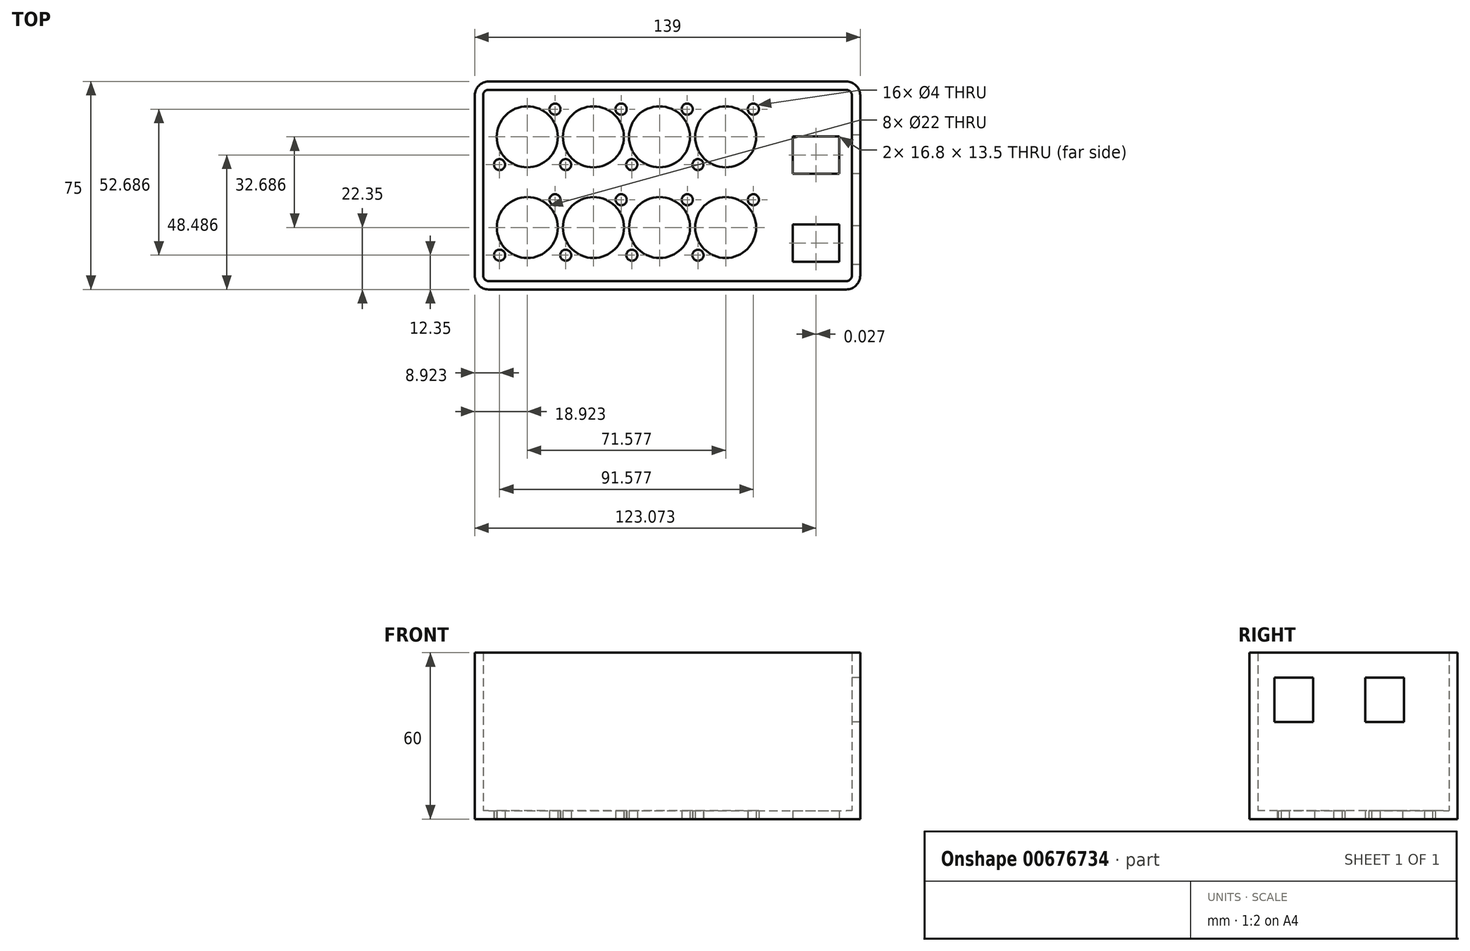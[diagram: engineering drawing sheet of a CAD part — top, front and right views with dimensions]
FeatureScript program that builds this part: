
annotation { "Feature Type Name" : "Feature", "Feature Type Description" : "" }
export const myFeature = defineFeature(function(context is Context, id is Id, definition is map)
    precondition{}
    {
        {
            var Q0;
            Q0=qCreatedBy(makeId("Top.planeOp"),FACE);
            var sketch = newSketch(context, id + "F0", { "sketchPlane" : qUnion([Q0])});
            skLineSegment(sketch, "E0.bottom", {"start": v(63.5, 18.5) * mm, "end": v(-63.5, 18.5) * mm, "construction": true});
            skLineSegment(sketch, "E0.top", {"start": v(66.5, -18.5) * mm, "end": v(-66.5, -18.5) * mm});
            skLineSegment(sketch, "E0.left", {"start": v(66.5, 15.5) * mm, "end": v(66.5, -18.5) * mm});
            skLineSegment(sketch, "E0.right", {"start": v(-66.5, 15.5) * mm, "end": v(-66.5, -18.5) * mm});
            skPoint(sketch, "E0.middle", {"position": v(0, 0) * mm});
            skLineSegment(sketch, "E1.top", {"start": v(45.2, 2) * mm, "end": v(62, 2) * mm});
            skCircle(sketch, "E2", {"center": v(21, 0.85) * mm, "radius": 11 * mm});
            skCircle(sketch, "E3", {"center": v(31, 10.85) * mm, "radius": 2 * mm});
            skCircle(sketch, "E4", {"center": v(11, -9.15) * mm, "radius": 2 * mm});
            skLineSegment(sketch, "E5", {"start": v(21, 0.85) * mm, "end": v(31, 10.85) * mm, "construction": true});
            skLineSegment(sketch, "E6", {"start": v(21, 0.85) * mm, "end": v(11, -9.15) * mm, "construction": true});
            skCircle(sketch, "E7", {"center": v(38.45, -6.1) * mm, "radius": 3.5 * mm, "construction": true});
            skLineSegment(sketch, "E8", {"start": v(64.5, -11.5) * mm, "end": v(-64.5, -11.5) * mm, "construction": true});
            skLineSegment(sketch, "E9.bottom", {"start": v(26.2, 19.15) * mm, "end": v(15.8, 19.15) * mm, "construction": true});
            skPoint(sketch, "E9.middle", {"position": v(21, 11.85) * mm});
            skLineSegment(sketch, "E10", {"start": v(15.8, 19.15) * mm, "end": v(15.8, 11.85) * mm, "construction": true});
            skLineSegment(sketch, "E11", {"start": v(15.8, 11.85) * mm, "end": v(15.8, 10.54) * mm, "construction": true});
            skLineSegment(sketch, "E12", {"start": v(15.8, 10.54) * mm, "end": v(26.2, 10.54) * mm, "construction": true});
            skLineSegment(sketch, "E13", {"start": v(26.2, 19.15) * mm, "end": v(26.2, 11.85) * mm, "construction": true});
            skLineSegment(sketch, "E14", {"start": v(26.2, 11.85) * mm, "end": v(26.2, 10.54) * mm, "construction": true});
            skCircle(sketch, "E15", {"center": v(21, -3.8) * mm, "radius": 6.5 * mm, "construction": true});
            skCircle(sketch, "E16.1.0.0", {"center": v(-2.85, -3.8) * mm, "radius": 6.5 * mm, "construction": true});
            skLineSegment(sketch, "E16.1.0.1", {"start": v(-2.85, 0.85) * mm, "end": v(7.15, 10.85) * mm, "construction": true});
            skLineSegment(sketch, "E16.1.0.2", {"start": v(2.35, 19.15) * mm, "end": v(-8.05, 19.15) * mm, "construction": true});
            skLineSegment(sketch, "E16.1.0.3", {"start": v(-2.85, 0.85) * mm, "end": v(-12.85, -9.15) * mm, "construction": true});
            skPoint(sketch, "E16.1.0.4", {"position": v(-2.85, 11.85) * mm});
            skLineSegment(sketch, "E16.1.0.5", {"start": v(2.35, 19.15) * mm, "end": v(2.35, 11.85) * mm, "construction": true});
            skCircle(sketch, "E16.1.0.6", {"center": v(-2.85, 0.85) * mm, "radius": 11 * mm});
            skCircle(sketch, "E16.1.0.7", {"center": v(7.15, 10.85) * mm, "radius": 2 * mm});
            skCircle(sketch, "E16.1.0.8", {"center": v(-12.85, -9.15) * mm, "radius": 2 * mm});
            skLineSegment(sketch, "E16.1.0.9", {"start": v(-8.05, 10.54) * mm, "end": v(2.35, 10.54) * mm, "construction": true});
            skLineSegment(sketch, "E16.1.0.10", {"start": v(-8.05, 19.15) * mm, "end": v(-8.05, 11.85) * mm, "construction": true});
            skLineSegment(sketch, "E16.1.0.11", {"start": v(2.35, 11.85) * mm, "end": v(2.35, 10.54) * mm, "construction": true});
            skLineSegment(sketch, "E16.1.0.12", {"start": v(-8.05, 11.85) * mm, "end": v(-8.05, 10.54) * mm, "construction": true});
            skCircle(sketch, "E16.2.0.0", {"center": v(-26.7, -3.8) * mm, "radius": 6.5 * mm, "construction": true});
            skLineSegment(sketch, "E16.2.0.1", {"start": v(-26.7, 0.85) * mm, "end": v(-16.7, 10.85) * mm, "construction": true});
            skLineSegment(sketch, "E16.2.0.2", {"start": v(-21.5, 19.15) * mm, "end": v(-31.9, 19.15) * mm, "construction": true});
            skLineSegment(sketch, "E16.2.0.3", {"start": v(-26.7, 0.85) * mm, "end": v(-36.7, -9.15) * mm, "construction": true});
            skPoint(sketch, "E16.2.0.4", {"position": v(-26.7, 11.85) * mm});
            skLineSegment(sketch, "E16.2.0.5", {"start": v(-21.5, 19.15) * mm, "end": v(-21.5, 11.85) * mm, "construction": true});
            skCircle(sketch, "E16.2.0.6", {"center": v(-26.7, 0.85) * mm, "radius": 11 * mm});
            skCircle(sketch, "E16.2.0.7", {"center": v(-16.7, 10.85) * mm, "radius": 2 * mm});
            skCircle(sketch, "E16.2.0.8", {"center": v(-36.7, -9.15) * mm, "radius": 2 * mm});
            skLineSegment(sketch, "E16.2.0.9", {"start": v(-31.9, 10.54) * mm, "end": v(-21.5, 10.54) * mm, "construction": true});
            skLineSegment(sketch, "E16.2.0.10", {"start": v(-31.9, 19.15) * mm, "end": v(-31.9, 11.85) * mm, "construction": true});
            skLineSegment(sketch, "E16.2.0.11", {"start": v(-21.5, 11.85) * mm, "end": v(-21.5, 10.54) * mm, "construction": true});
            skLineSegment(sketch, "E16.2.0.12", {"start": v(-31.9, 11.85) * mm, "end": v(-31.9, 10.54) * mm, "construction": true});
            skCircle(sketch, "E16.3.0.0", {"center": v(-50.55, -3.8) * mm, "radius": 6.5 * mm, "construction": true});
            skLineSegment(sketch, "E16.3.0.1", {"start": v(-50.55, 0.85) * mm, "end": v(-40.55, 10.85) * mm, "construction": true});
            skLineSegment(sketch, "E16.3.0.2", {"start": v(-45.35, 19.15) * mm, "end": v(-55.75, 19.15) * mm, "construction": true});
            skLineSegment(sketch, "E16.3.0.3", {"start": v(-50.55, 0.85) * mm, "end": v(-60.55, -9.15) * mm, "construction": true});
            skPoint(sketch, "E16.3.0.4", {"position": v(-50.55, 11.85) * mm});
            skLineSegment(sketch, "E16.3.0.5", {"start": v(-45.35, 19.15) * mm, "end": v(-45.35, 11.85) * mm, "construction": true});
            skCircle(sketch, "E16.3.0.6", {"center": v(-50.55, 0.85) * mm, "radius": 11 * mm});
            skCircle(sketch, "E16.3.0.7", {"center": v(-40.55, 10.85) * mm, "radius": 2 * mm});
            skCircle(sketch, "E16.3.0.8", {"center": v(-60.55, -9.15) * mm, "radius": 2 * mm});
            skLineSegment(sketch, "E16.3.0.9", {"start": v(-55.75, 10.54) * mm, "end": v(-45.35, 10.54) * mm, "construction": true});
            skLineSegment(sketch, "E16.3.0.10", {"start": v(-55.75, 19.15) * mm, "end": v(-55.75, 11.85) * mm, "construction": true});
            skLineSegment(sketch, "E16.3.0.11", {"start": v(-45.35, 11.85) * mm, "end": v(-45.35, 10.54) * mm, "construction": true});
            skLineSegment(sketch, "E16.3.0.12", {"start": v(-55.75, 11.85) * mm, "end": v(-55.75, 10.54) * mm, "construction": true});
            skLineSegment(sketch, "E16.direction1", {"start": v(21, 0.85) * mm, "end": v(-2.85, 0.85) * mm, "construction": true});
            skLineSegment(sketch, "E17.0", {"start": v(63.5, 21.5) * mm, "end": v(-63.5, 21.5) * mm, "construction": true});
            skLineSegment(sketch, "E17.1", {"start": v(69.5, 15.5) * mm, "end": v(69.5, -15.5) * mm});
            skLineSegment(sketch, "E17.2", {"start": v(63.5, -21.5) * mm, "end": v(-63.5, -21.5) * mm});
            skLineSegment(sketch, "E17.3", {"start": v(-69.5, 15.5) * mm, "end": v(-69.5, -15.5) * mm});
            skPoint(sketch, "E18.visualSharp", {"position": v(-69.5, 21.5) * mm});
            skPoint(sketch, "E19.visualSharp", {"position": v(69.5, 21.5) * mm});
            skPoint(sketch, "E20.visualSharp", {"position": v(66.5, 18.5) * mm});
            skPoint(sketch, "E21.visualSharp", {"position": v(-69.5, -21.5) * mm});
            skPoint(sketch, "E22.visualSharp", {"position": v(69.5, -21.5) * mm});
            skLineSegment(sketch, "E23", {"start": v(45.2, 2) * mm, "end": v(45.2, -11.5) * mm});
            skLineSegment(sketch, "E24", {"start": v(45.2, -11.5) * mm, "end": v(62, -11.5) * mm});
            skLineSegment(sketch, "E25", {"start": v(62, -11.5) * mm, "end": v(62, 2) * mm});
            skPoint(sketch, "E26.middle", {"position": v(-0.03, 32.69) * mm});
            skLineSegment(sketch, "E27.top", {"start": v(45.17, 33.74) * mm, "end": v(61.97, 33.74) * mm});
            skCircle(sketch, "E28", {"center": v(20.97, 33.54) * mm, "radius": 11 * mm});
            skCircle(sketch, "E29", {"center": v(30.97, 43.54) * mm, "radius": 2 * mm});
            skCircle(sketch, "E30", {"center": v(10.97, 23.54) * mm, "radius": 2 * mm});
            skLineSegment(sketch, "E31", {"start": v(20.97, 33.54) * mm, "end": v(30.97, 43.54) * mm, "construction": true});
            skLineSegment(sketch, "E32", {"start": v(20.97, 33.54) * mm, "end": v(10.97, 23.54) * mm, "construction": true});
            skCircle(sketch, "E33", {"center": v(38.42, 26.59) * mm, "radius": 3.5 * mm, "construction": true});
            skPoint(sketch, "E34.middle", {"position": v(20.97, 44.54) * mm});
            skLineSegment(sketch, "E35", {"start": v(15.77, 44.54) * mm, "end": v(15.77, 43.23) * mm, "construction": true});
            skLineSegment(sketch, "E36", {"start": v(15.77, 43.23) * mm, "end": v(26.17, 43.23) * mm, "construction": true});
            skLineSegment(sketch, "E37", {"start": v(26.17, 44.54) * mm, "end": v(26.17, 43.23) * mm, "construction": true});
            skCircle(sketch, "E38", {"center": v(20.97, 28.89) * mm, "radius": 6.5 * mm, "construction": true});
            skCircle(sketch, "E39.1.0.0", {"center": v(-2.88, 28.89) * mm, "radius": 6.5 * mm, "construction": true});
            skLineSegment(sketch, "E39.1.0.1", {"start": v(-2.88, 33.54) * mm, "end": v(7.12, 43.54) * mm, "construction": true});
            skLineSegment(sketch, "E39.1.0.3", {"start": v(-2.88, 33.54) * mm, "end": v(-12.88, 23.54) * mm, "construction": true});
            skPoint(sketch, "E39.1.0.4", {"position": v(-2.88, 44.54) * mm});
            skCircle(sketch, "E39.1.0.6", {"center": v(-2.88, 33.54) * mm, "radius": 11 * mm});
            skCircle(sketch, "E39.1.0.7", {"center": v(7.12, 43.54) * mm, "radius": 2 * mm});
            skCircle(sketch, "E39.1.0.8", {"center": v(-12.88, 23.54) * mm, "radius": 2 * mm});
            skLineSegment(sketch, "E39.1.0.9", {"start": v(-8.08, 43.23) * mm, "end": v(2.32, 43.23) * mm, "construction": true});
            skLineSegment(sketch, "E39.1.0.11", {"start": v(2.32, 44.54) * mm, "end": v(2.32, 43.23) * mm, "construction": true});
            skLineSegment(sketch, "E39.1.0.12", {"start": v(-8.08, 44.54) * mm, "end": v(-8.08, 43.23) * mm, "construction": true});
            skCircle(sketch, "E39.2.0.0", {"center": v(-26.73, 28.89) * mm, "radius": 6.5 * mm, "construction": true});
            skLineSegment(sketch, "E39.2.0.1", {"start": v(-26.73, 33.54) * mm, "end": v(-16.73, 43.54) * mm, "construction": true});
            skLineSegment(sketch, "E39.2.0.3", {"start": v(-26.73, 33.54) * mm, "end": v(-36.73, 23.54) * mm, "construction": true});
            skPoint(sketch, "E39.2.0.4", {"position": v(-26.73, 44.54) * mm});
            skCircle(sketch, "E39.2.0.6", {"center": v(-26.73, 33.54) * mm, "radius": 11 * mm});
            skCircle(sketch, "E39.2.0.7", {"center": v(-16.73, 43.54) * mm, "radius": 2 * mm});
            skCircle(sketch, "E39.2.0.8", {"center": v(-36.73, 23.54) * mm, "radius": 2 * mm});
            skLineSegment(sketch, "E39.2.0.9", {"start": v(-31.93, 43.23) * mm, "end": v(-21.53, 43.23) * mm, "construction": true});
            skLineSegment(sketch, "E39.2.0.11", {"start": v(-21.53, 44.54) * mm, "end": v(-21.53, 43.23) * mm, "construction": true});
            skLineSegment(sketch, "E39.2.0.12", {"start": v(-31.93, 44.54) * mm, "end": v(-31.93, 43.23) * mm, "construction": true});
            skCircle(sketch, "E39.3.0.0", {"center": v(-50.58, 28.89) * mm, "radius": 6.5 * mm, "construction": true});
            skLineSegment(sketch, "E39.3.0.1", {"start": v(-50.58, 33.54) * mm, "end": v(-40.58, 43.54) * mm, "construction": true});
            skLineSegment(sketch, "E39.3.0.3", {"start": v(-50.58, 33.54) * mm, "end": v(-60.58, 23.54) * mm, "construction": true});
            skPoint(sketch, "E39.3.0.4", {"position": v(-50.58, 44.54) * mm});
            skCircle(sketch, "E39.3.0.6", {"center": v(-50.58, 33.54) * mm, "radius": 11 * mm});
            skCircle(sketch, "E39.3.0.7", {"center": v(-40.58, 43.54) * mm, "radius": 2 * mm});
            skCircle(sketch, "E39.3.0.8", {"center": v(-60.58, 23.54) * mm, "radius": 2 * mm});
            skLineSegment(sketch, "E39.3.0.9", {"start": v(-55.78, 43.23) * mm, "end": v(-45.38, 43.23) * mm, "construction": true});
            skLineSegment(sketch, "E39.3.0.11", {"start": v(-45.38, 44.54) * mm, "end": v(-45.38, 43.23) * mm, "construction": true});
            skLineSegment(sketch, "E39.3.0.12", {"start": v(-55.78, 44.54) * mm, "end": v(-55.78, 43.23) * mm, "construction": true});
            skLineSegment(sketch, "E39.direction1", {"start": v(20.97, 33.54) * mm, "end": v(-2.88, 33.54) * mm, "construction": true});
            skLineSegment(sketch, "E40", {"start": v(45.17, 33.74) * mm, "end": v(45.17, 20.24) * mm});
            skLineSegment(sketch, "E41", {"start": v(45.17, 20.24) * mm, "end": v(61.97, 20.24) * mm});
            skLineSegment(sketch, "E42", {"start": v(61.97, 20.24) * mm, "end": v(61.97, 33.74) * mm});
            skLineSegment(sketch, "E43", {"start": v(-69.5, 15.5) * mm, "end": v(-69.5, 53.5) * mm});
            skLineSegment(sketch, "E44", {"start": v(-69.5, 53.5) * mm, "end": v(69.5, 53.5) * mm});
            skLineSegment(sketch, "E45", {"start": v(69.5, 53.5) * mm, "end": v(69.5, 15.5) * mm});
            skLineSegment(sketch, "E46", {"start": v(-66.5, 15.5) * mm, "end": v(-66.5, 50.5) * mm});
            skLineSegment(sketch, "E47", {"start": v(-66.5, 50.5) * mm, "end": v(66.5, 50.5) * mm});
            skLineSegment(sketch, "E48", {"start": v(66.5, 50.5) * mm, "end": v(66.5, 15.5) * mm});
            skLineSegment(sketch, "E49", {"start": v(-69.5, -15.5) * mm, "end": v(-69.5, -21.5) * mm});
            skLineSegment(sketch, "E50", {"start": v(-63.5, -21.5) * mm, "end": v(-69.5, -21.5) * mm});
            skLineSegment(sketch, "E51", {"start": v(63.5, -21.5) * mm, "end": v(69.5, -21.5) * mm});
            skLineSegment(sketch, "E52", {"start": v(69.5, -15.5) * mm, "end": v(69.5, -21.5) * mm});
            skSolve(sketch);
        }
        {
            var Q0;
            Q0=makeQuery(id+"F0.imprint","IMPRINT",FACE,{"disambiguationData":[TD([[makeQuery(id+"F0.imprint","IMPRINT",EDGE,{"derivedFrom":sQuery(id+"F0.wireOp",EDGE,"E0.top")}),-1.0]])]});
            extrude(context, id + "F1", {"entities" : qUnion([Q0]), "depth" : 3 * mm, "offsetDistance" : 25 * mm});
        }
        {
            var Q0;
            Q0=makeQuery(id+"F0.imprint","IMPRINT",FACE,{"disambiguationData":[TD([[makeQuery(id+"F0.imprint","IMPRINT",EDGE,{"derivedFrom":sQuery(id+"F0.wireOp",EDGE,"E0.top")}),1.0]])]});
            extrude(context, id + "F2", {"entities" : qUnion([Q0]), "operationType" : NewBodyOperationType.ADD, "depth" : 60 * mm, "offsetDistance" : 25 * mm});
        }
        {
            var Q0;
            Q0=qCreatedBy(makeId("Right.planeOp"),FACE);
            var sketch = newSketch(context, id + "F3", { "sketchPlane" : qUnion([Q0])});
            skLineSegment(sketch, "E53.bottom", {"start": v(-12.5, 35) * mm, "end": v(1.5, 35) * mm});
            skLineSegment(sketch, "E53.top", {"start": v(-12.5, 51) * mm, "end": v(1.5, 51) * mm});
            skLineSegment(sketch, "E53.left", {"start": v(-12.5, 35) * mm, "end": v(-12.5, 51) * mm});
            skLineSegment(sketch, "E53.right", {"start": v(1.5, 35) * mm, "end": v(1.5, 51) * mm});
            skLineSegment(sketch, "E54.bottom", {"start": v(20.24, 35) * mm, "end": v(34.24, 35) * mm});
            skLineSegment(sketch, "E54.top", {"start": v(20.24, 51) * mm, "end": v(34.24, 51) * mm});
            skLineSegment(sketch, "E54.left", {"start": v(20.24, 35) * mm, "end": v(20.24, 51) * mm});
            skLineSegment(sketch, "E54.right", {"start": v(34.24, 35) * mm, "end": v(34.24, 51) * mm});
            skSolve(sketch);
        }
        {
            var Q0;
            Q0=qSketchRegion(id+"F3",true);
            extrude(context, id + "F4", {"entities" : qUnion([Q0]), "operationType" : NewBodyOperationType.REMOVE, "endBound" : BoundingType.THROUGH_ALL, "depth" : 25 * mm, "offsetDistance" : 25 * mm});
        }
        {
            var Q0;
            Q0=makeQuery(id+"F2.opExtrude","SWEPT_EDGE",EDGE,{"disambiguationData":[OSD([sQuery(id+"F0.wireOp",EDGE,"E0.top"),sQuery(id+"F0.wireOp",EDGE,"E0.left")])]});
            var Q1;
            Q1=makeQuery(id+"F2.opExtrude","SWEPT_EDGE",EDGE,{"disambiguationData":[OSD([sQuery(id+"F0.wireOp",EDGE,"E0.top"),sQuery(id+"F0.wireOp",EDGE,"E0.right")])]});
            var Q2;
            Q2=makeQuery(id+"F2.opExtrude","SWEPT_EDGE",EDGE,{"disambiguationData":[OSD([sQuery(id+"F0.wireOp",EDGE,"E46"),sQuery(id+"F0.wireOp",EDGE,"E47")])]});
            var Q3;
            Q3=makeQuery(id+"F2.opExtrude","SWEPT_EDGE",EDGE,{"disambiguationData":[OSD([sQuery(id+"F0.wireOp",EDGE,"E47"),sQuery(id+"F0.wireOp",EDGE,"E48")])]});
            var Q4;
            Q4=makeQuery(id+"F1.opExtrude","CAP_EDGE",EDGE,{"disambiguationData":[OSD([sQuery(id+"F0.wireOp",EDGE,"E0.left"),sQuery(id+"F0.wireOp",EDGE,"E48")])],"isStart":false});
            var Q5;
            Q5=makeQuery(id+"F1.opExtrude","CAP_EDGE",EDGE,{"disambiguationData":[OSD([sQuery(id+"F0.wireOp",EDGE,"E47")])],"isStart":false});
            var Q6;
            Q6=makeQuery(id+"F1.opExtrude","CAP_EDGE",EDGE,{"disambiguationData":[OSD([sQuery(id+"F0.wireOp",EDGE,"E0.top")])],"isStart":false});
            var Q7;
            Q7=makeQuery(id+"F1.opExtrude","CAP_EDGE",EDGE,{"disambiguationData":[OSD([sQuery(id+"F0.wireOp",EDGE,"E0.right"),sQuery(id+"F0.wireOp",EDGE,"E46")])],"isStart":false});
            fillet(context, id + "F5", {"entities" : qUnion([Q0, Q1, Q2, Q3, Q4, Q5, Q6, Q7]), "radius" : 2 * mm, "tangentPropagation" : true, "allowEdgeOverflow" : false});
        }
        {
            var Q0;
            Q0=makeQuery(id+"F2.opExtrude","SWEPT_EDGE",EDGE,{"disambiguationData":[OSD([sQuery(id+"F0.wireOp",EDGE,"E51"),sQuery(id+"F0.wireOp",EDGE,"E52")])]});
            var Q1;
            Q1=makeQuery(id+"F2.opExtrude","SWEPT_EDGE",EDGE,{"disambiguationData":[OSD([sQuery(id+"F0.wireOp",EDGE,"E44"),sQuery(id+"F0.wireOp",EDGE,"E45")])]});
            var Q2;
            Q2=makeQuery(id+"F2.opExtrude","SWEPT_EDGE",EDGE,{"disambiguationData":[OSD([sQuery(id+"F0.wireOp",EDGE,"E43"),sQuery(id+"F0.wireOp",EDGE,"E44")])]});
            var Q3;
            Q3=makeQuery(id+"F2.opExtrude","SWEPT_EDGE",EDGE,{"disambiguationData":[OSD([sQuery(id+"F0.wireOp",EDGE,"E49"),sQuery(id+"F0.wireOp",EDGE,"E50")])]});
            fillet(context, id + "F6", {"entities" : qUnion([Q0, Q1, Q2, Q3]), "radius" : 5 * mm, "tangentPropagation" : true, "allowEdgeOverflow" : false});
        }
    });
